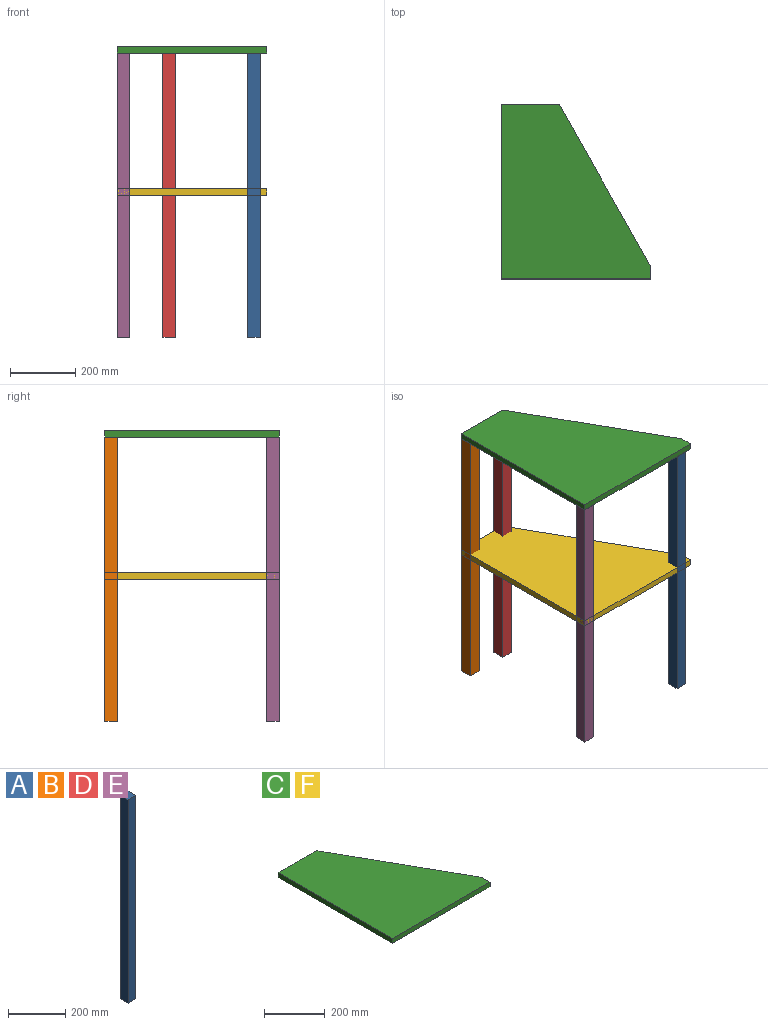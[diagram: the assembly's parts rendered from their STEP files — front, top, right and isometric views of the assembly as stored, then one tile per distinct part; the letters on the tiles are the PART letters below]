
ASSEMBLY  parts=6 mates=9
PART A: 6 faces, bbox 38.1x38.1x870 mm
  f0: plane 869.95x38.1mm, normal (-1,0,0), area 33145.1mm2, adj f1,f3,f4,f5
  f1: plane 869.95x38.1mm, normal (0,-1,0), area 33145.1mm2, adj f0,f2,f4,f5
  f2: plane 869.95x38.1mm, normal (1,0,0), area 33145.1mm2, adj f1,f3,f4,f5
  f3: plane 869.95x38.1mm, normal (0,1,0), area 33145.1mm2, adj f0,f2,f4,f5
  f4: plane 38.1x38.1mm, normal (0,0,1), area 1451.6mm2, adj f0,f1,f2,f3
  f5: plane 38.1x38.1mm, normal (0,0,-1), area 1451.6mm2, adj f0,f1,f2,f3
PART B: same geometry as A
PART C: 7 faces, bbox 457.2x533.4x19.1 mm
  f0: plane 533.4x19.05mm, normal (-1,0,0), area 10161.3mm2, adj f1,f4,f5,f6
  f1: plane 457.2x19.05mm, normal (0,-1,0), area 8709.7mm2, adj f0,f2,f5,f6
  f2: plane 38.1x19.05mm, normal (1,0,0), area 725.8mm2, adj f1,f3,f5,f6
  f3: plane 495.3x279.4mm, normal (0.87,0.49,0), area 10833.2mm2, adj f2,f4,f5,f6
  f4: plane 177.8x19.05mm, normal (0,1,0), area 3387.1mm2, adj f0,f3,f5,f6
  f5: plane 533.4x457.2mm, normal (0,0,1), area 174677.1mm2, adj f0,f1,f2,f3,f4
  f6: plane 533.4x457.2mm, normal (0,0,-1), area 174677.1mm2, adj f0,f1,f2,f3,f4
PART D: same geometry as A
PART E: same geometry as A
PART F: same geometry as C
PLACE A t=(605.33,-34,-280.98)mm
PLACE B t=(206.18,461.3,-280.98)mm
PLACE C t=(206.18,-34,588.97)mm fixed
PLACE D t=(345.88,461.3,-280.98)mm
PLACE E t=(206.18,-34,-280.98)mm
PLACE F t=(206.18,-34,153.99)mm
MATE parallel E.f1 <-> C.f1  axis (0,-1,0) through (225.23,-34,153.99)mm
MATE parallel F.f1 <-> E.f1  axis (0,-1,0) through (206.18,-34,153.99)mm
MATE parallel E.f0 <-> C.f0  axis (-1,0,0) through (206.18,-14.95,153.99)mm
MATE planar A.f4 <-> C.f6  axis (0,0,1) through (643.43,-34,588.97)mm
MATE planar D.f4 <-> C.f6  axis (0,0,1) through (383.98,499.4,588.97)mm
MATE planar F.f1 <-> A.f1  axis (0,-1,0) through (663.38,-34,153.99)mm
MATE planar E.f4 <-> C.f6  axis (0,0,1) through (225.23,-14.95,588.97)mm
MATE parallel F.f5 <-> C.f6  axis (0,0,1) through (206.18,499.4,173.04)mm
MATE planar B.f4 <-> C.f6  axis (0,0,1) through (206.18,499.4,588.97)mm
